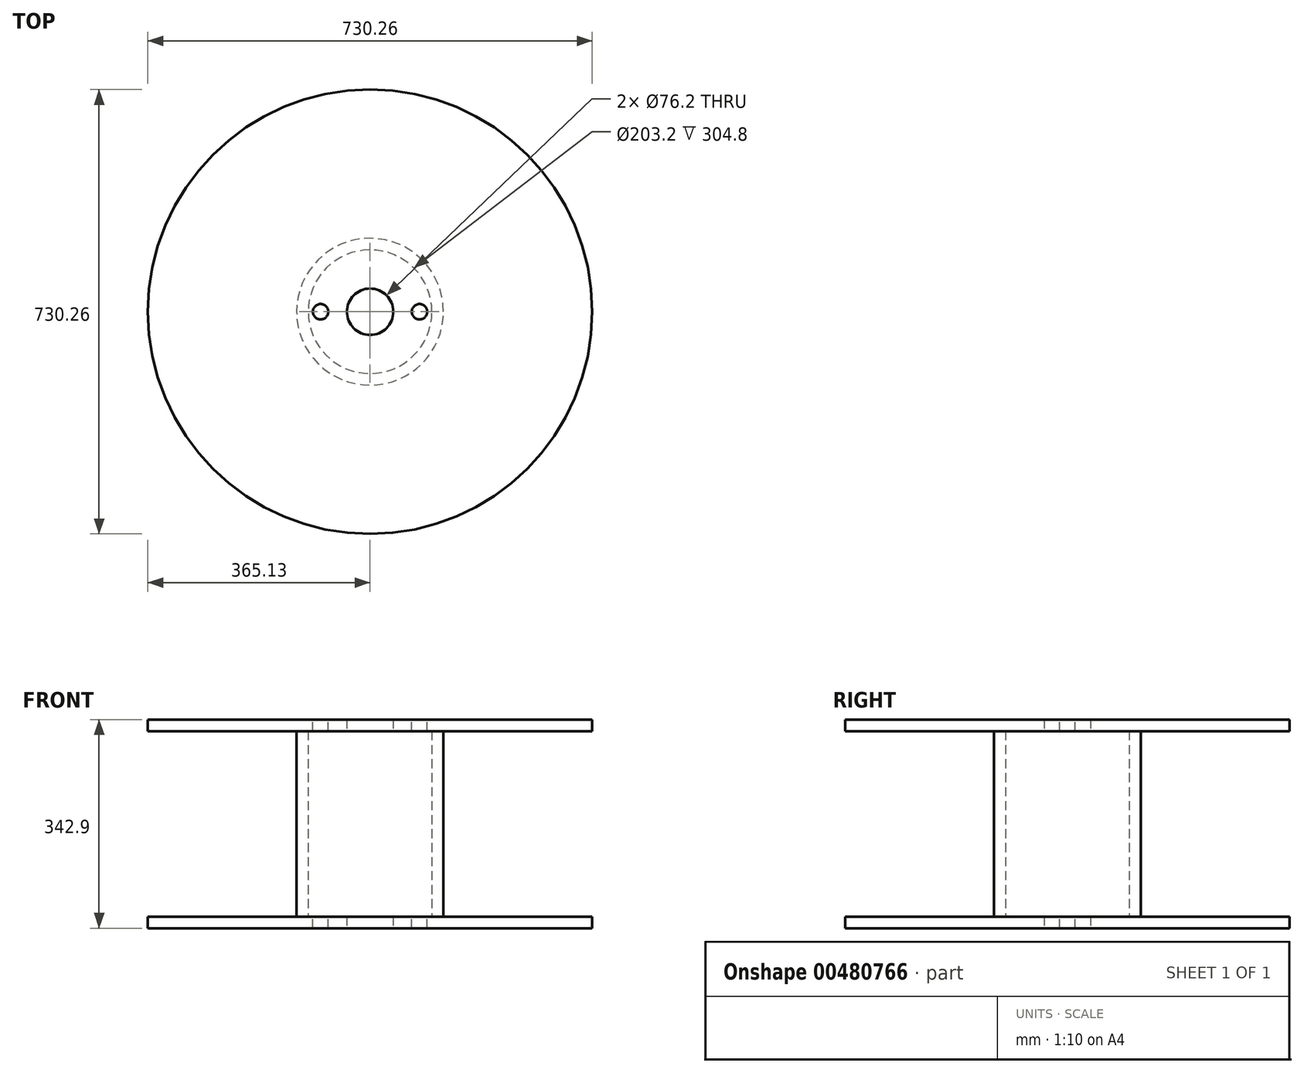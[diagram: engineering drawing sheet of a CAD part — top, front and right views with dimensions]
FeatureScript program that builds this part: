
annotation { "Feature Type Name" : "Feature", "Feature Type Description" : "" }
export const myFeature = defineFeature(function(context is Context, id is Id, definition is map)
    precondition{}
    {
        {
            var Q0;
            Q0=qCreatedBy(makeId("Top.planeOp"),FACE);
            var sketch = newSketch(context, id + "F0", { "sketchPlane" : qUnion([Q0])});
            skCircle(sketch, "E0", {"center": v(0, 0) * mm, "radius": 365.13 * mm});
            skSolve(sketch);
        }
        {
            var Q0;
            Q0 = qSketchRegion(id + "F0", true);
            extrude(context, id + "F1", {"entities" : qUnion([Q0]), "depth" : 19.05 * mm, "offsetDistance" : 25.4 * mm});
        }
        {
            var Q0;
            Q0=makeQuery(id+"F1.opExtrude","CAP_FACE",FACE,{"disambiguationData":[OSD([sQuery(id+"F0.wireOp",EDGE,"E0")])],"isStart":false});
            var sketch = newSketch(context, id + "F2", { "sketchPlane" : qUnion([Q0])});
            skCircle(sketch, "E1", {"center": v(0, 0) * mm, "radius": 101.6 * mm});
            skCircle(sketch, "E2", {"center": v(0, 0) * mm, "radius": 120.65 * mm});
            skSolve(sketch);
        }
        {
            var Q0;
            Q0=makeQuery(id+"F2.imprint","IMPRINT",FACE,{"disambiguationData":[TD([[makeQuery(id+"F2.imprint","IMPRINT",EDGE,{"derivedFrom":sQuery(id+"F2.wireOp",EDGE,"E1")}),-1.0]])]});
            extrude(context, id + "F3", {"entities" : qUnion([Q0]), "operationType" : NewBodyOperationType.ADD, "depth" : 304.8 * mm, "offsetDistance" : 25.4 * mm});
        }
        {
            var Q0;
            Q0=makeQuery(id+"F3.opExtrude","CAP_FACE",FACE,{"disambiguationData":[OSD([sQuery(id+"F2.wireOp",EDGE,"E1"),sQuery(id+"F2.wireOp",EDGE,"E2")])],"isStart":false});
            var sketch = newSketch(context, id + "F4", { "sketchPlane" : qUnion([Q0])});
            skCircle(sketch, "E3", {"center": v(0, 0) * mm, "radius": 365.13 * mm});
            skSolve(sketch);
        }
        {
            var Q0;
            Q0=makeQuery(id+"F4.imprint","IMPRINT",FACE,{"disambiguationData":[TD([[makeQuery(id+"F4.imprint","IMPRINT",EDGE,{"derivedFrom":sQuery(id+"F4.wireOp",EDGE,"E3")}),1.0]])]});
            var Q1;
            Q1=makeQuery(id+"F4.imprint","IMPRINT",FACE,{"disambiguationData":[TD([[makeQuery(id+"F4.imprint","IMPRINT",EDGE,{"derivedFrom":makeQuery(id+"F3.opExtrude","CAP_EDGE",EDGE,{"disambiguationData":[OSD([sQuery(id+"F2.wireOp",EDGE,"E1")])],"isStart":false})}),1.0]])]});
            var Q2;
            Q2=makeQuery(id+"F4.imprint","IMPRINT",FACE,{"disambiguationData":[TD([[makeQuery(id+"F4.imprint","IMPRINT",EDGE,{"derivedFrom":makeQuery(id+"F3.opExtrude","CAP_EDGE",EDGE,{"disambiguationData":[OSD([sQuery(id+"F2.wireOp",EDGE,"E1")])],"isStart":false})}),-1.0]])]});
            extrude(context, id + "F5", {"entities" : qUnion([Q0, Q1, Q2]), "operationType" : NewBodyOperationType.ADD, "depth" : 19.05 * mm, "offsetDistance" : 25.4 * mm});
        }
        {
            var Q0;
            Q0=makeQuery(id+"F1.opExtrude","CAP_FACE",FACE,{"disambiguationData":[OSD([sQuery(id+"F0.wireOp",EDGE,"E0")])],"isStart":true});
            var sketch = newSketch(context, id + "F6", { "sketchPlane" : qUnion([Q0])});
            skCircle(sketch, "E4", {"center": v(0, 0) * mm, "radius": 38.1 * mm});
            skSolve(sketch);
        }
        {
            var Q0;
            Q0=makeQuery(id+"F6.imprint","IMPRINT",FACE,{"disambiguationData":[TD([[makeQuery(id+"F6.imprint","IMPRINT",EDGE,{"derivedFrom":sQuery(id+"F6.wireOp",EDGE,"E4")}),1.0]])]});
            extrude(context, id + "F7", {"entities" : qUnion([Q0]), "operationType" : NewBodyOperationType.REMOVE, "oppositeDirection" : true, "depth" : 355.6 * mm, "offsetDistance" : 25.4 * mm});
        }
        {
            var Q0;
            Q0=makeQuery(id+"F5.opExtrude","CAP_FACE",FACE,{"disambiguationData":[OSD([sQuery(id+"F4.wireOp",EDGE,"E3")])],"isStart":false});
            var sketch = newSketch(context, id + "F8", { "sketchPlane" : qUnion([Q0])});
            skCircle(sketch, "E5", {"center": v(-81.28, 0) * mm, "radius": 12.7 * mm});
            skCircle(sketch, "E6", {"center": v(81.28, 0) * mm, "radius": 12.7 * mm});
            skSolve(sketch);
        }
        {
            var Q0;
            Q0=makeQuery(id+"F8.imprint","IMPRINT",FACE,{"disambiguationData":[TD([[makeQuery(id+"F8.imprint","IMPRINT",EDGE,{"derivedFrom":sQuery(id+"F8.wireOp",EDGE,"E5")}),1.0]])]});
            var Q1;
            Q1=makeQuery(id+"F8.imprint","IMPRINT",FACE,{"disambiguationData":[TD([[makeQuery(id+"F8.imprint","IMPRINT",EDGE,{"derivedFrom":sQuery(id+"F8.wireOp",EDGE,"E6")}),1.0]])]});
            extrude(context, id + "F9", {"entities" : qUnion([Q0, Q1]), "operationType" : NewBodyOperationType.REMOVE, "oppositeDirection" : true, "depth" : 355.6 * mm, "offsetDistance" : 25.4 * mm});
        }
    });
